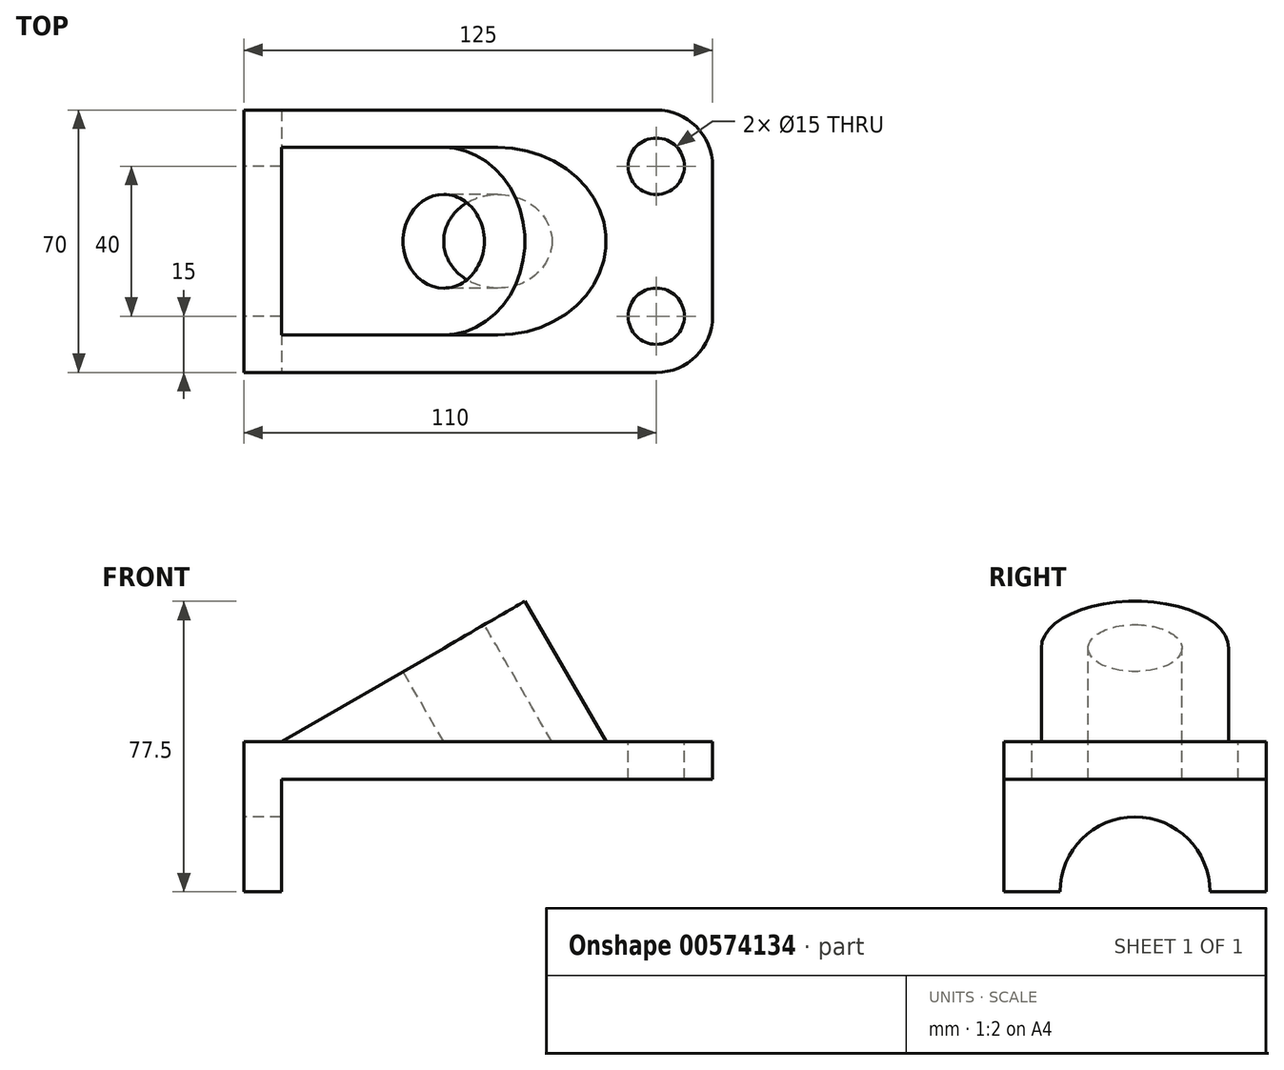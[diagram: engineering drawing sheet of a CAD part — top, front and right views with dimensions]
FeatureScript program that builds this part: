
annotation { "Feature Type Name" : "Feature", "Feature Type Description" : "" }
export const myFeature = defineFeature(function(context is Context, id is Id, definition is map)
    precondition{}
    {
        {
            var Q0;
            Q0=qCreatedBy(makeId("Front.planeOp"),FACE);
            var sketch = newSketch(context, id + "F0", { "sketchPlane" : qUnion([Q0])});
            skLineSegment(sketch, "E0.bottom", {"start": v(62.5, 20) * mm, "end": v(-62.5, 20) * mm});
            skLineSegment(sketch, "E0.top", {"start": v(62.5, -20) * mm, "end": v(-62.5, -20) * mm});
            skLineSegment(sketch, "E0.left", {"start": v(62.5, 20) * mm, "end": v(62.5, -20) * mm});
            skLineSegment(sketch, "E0.right", {"start": v(-62.5, 20) * mm, "end": v(-62.5, -20) * mm});
            skPoint(sketch, "E0.middle", {"position": v(0, 0) * mm});
            skSolve(sketch);
        }
        {
            var Q0;
            Q0=makeQuery(id+"F0.imprint","IMPRINT",FACE,{"disambiguationData":[TD([[makeQuery(id+"F0.imprint","IMPRINT",EDGE,{"derivedFrom":sQuery(id+"F0.wireOp",EDGE,"E0.bottom")}),1.0]])]});
            extrude(context, id + "F1", {"entities" : qUnion([Q0]), "depth" : 70 * mm, "offsetDistance" : 25 * mm});
        }
        {
            var Q0;
            Q0=makeQuery(id+"F1.opExtrude","SWEPT_FACE",FACE,{"disambiguationData":[OSD([sQuery(id+"F0.wireOp",EDGE,"E0.right")])]});
            var sketch = newSketch(context, id + "F2", { "sketchPlane" : qUnion([Q0])});
            skLineSegment(sketch, "E1", {"start": v(35, -20) * mm, "end": v(35, 0) * mm, "construction": true});
            skCircle(sketch, "E2", {"center": v(35, -20) * mm, "radius": 20 * mm});
            skLineSegment(sketch, "E3", {"start": v(0, -20) * mm, "end": v(15, -20) * mm, "construction": true});
            skLineSegment(sketch, "E4", {"start": v(70, -20) * mm, "end": v(55, -20) * mm, "construction": true});
            skSolve(sketch);
        }
        {
            var Q0;
            {var subQ0=sQuery(id+"F2.wireOp",EDGE,"E2");var subQ1=makeQuery(id+"F1.opExtrude","SWEPT_EDGE",EDGE,{"disambiguationData":[OSD([sQuery(id+"F0.wireOp",EDGE,"E0.top"),sQuery(id+"F0.wireOp",EDGE,"E0.right")])]});var subQ2=makeQuery(id+"F2.imprint","INTERSECT",VERTEX,{"disambiguationData":[OD(0.0)],"derivedFrom":[subQ1,subQ0]});Q0=makeQuery(id+"F2.imprint","IMPRINT",FACE,{"disambiguationData":[TD([[makeQuery(id+"F2.imprint","IMPRINT",EDGE,{"disambiguationData":[TD([[subQ2,1.0]])],"derivedFrom":subQ0}),1.0]])]});}
            var Q1;
            {var subQ0=sQuery(id+"F2.wireOp",EDGE,"E2");var subQ1=makeQuery(id+"F1.opExtrude","SWEPT_EDGE",EDGE,{"disambiguationData":[OSD([sQuery(id+"F0.wireOp",EDGE,"E0.top"),sQuery(id+"F0.wireOp",EDGE,"E0.right")])]});var subQ2=makeQuery(id+"F2.imprint","INTERSECT",VERTEX,{"disambiguationData":[OD(0.0)],"derivedFrom":[subQ1,subQ0]});Q1=makeQuery(id+"F2.imprint","IMPRINT",FACE,{"disambiguationData":[TD([[makeQuery(id+"F2.imprint","IMPRINT",EDGE,{"disambiguationData":[TD([[subQ2,-1.0]])],"derivedFrom":subQ0}),1.0]])]});}
            extrude(context, id + "F3", {"entities" : qUnion([Q0, Q1]), "operationType" : NewBodyOperationType.REMOVE, "endBound" : BoundingType.THROUGH_ALL, "oppositeDirection" : true, "depth" : 25 * mm, "offsetDistance" : 25 * mm});
        }
        {
            var Q0;
            Q0=makeQuery(id+"F1.opExtrude","CAP_FACE",FACE,{"disambiguationData":[OSD([sQuery(id+"F0.wireOp",EDGE,"E0.bottom"),sQuery(id+"F0.wireOp",EDGE,"E0.top"),sQuery(id+"F0.wireOp",EDGE,"E0.left"),sQuery(id+"F0.wireOp",EDGE,"E0.right")])],"isStart":false});
            var sketch = newSketch(context, id + "F4", { "sketchPlane" : qUnion([Q0])});
            skLineSegment(sketch, "E5", {"start": v(-62.5, -20) * mm, "end": v(-52.5, -20) * mm});
            skLineSegment(sketch, "E6", {"start": v(-52.5, -20) * mm, "end": v(-52.5, 10) * mm});
            skLineSegment(sketch, "E7", {"start": v(-52.5, 10) * mm, "end": v(62.5, 10) * mm});
            skSolve(sketch);
        }
        {
            var Q0;
            {var subQ0=sQuery(id+"F4.wireOp",EDGE,"E6");Q0=makeQuery(id+"F4.imprint","IMPRINT",FACE,{"disambiguationData":[TD([[makeQuery(id+"F4.imprint","IMPRINT",EDGE,{"derivedFrom":subQ0}),-1.0]])]});}
            extrude(context, id + "F5", {"entities" : qUnion([Q0]), "operationType" : NewBodyOperationType.REMOVE, "endBound" : BoundingType.THROUGH_ALL, "oppositeDirection" : true, "depth" : 25 * mm, "offsetDistance" : 25 * mm});
        }
        {
            var Q0;
            Q0=makeQuery(id+"F1.opExtrude","CAP_EDGE",EDGE,{"disambiguationData":[OSD([sQuery(id+"F0.wireOp",EDGE,"E0.left")])],"isStart":false});
            var Q1;
            Q1=makeQuery(id+"F1.opExtrude","CAP_EDGE",EDGE,{"disambiguationData":[OSD([sQuery(id+"F0.wireOp",EDGE,"E0.left")])],"isStart":true});
            fillet(context, id + "F6", {"entities" : qUnion([Q0, Q1]), "radius" : 15 * mm, "tangentPropagation" : true, "allowEdgeOverflow" : false});
        }
        {
            var Q0;
            Q0=makeQuery(id+"F1.opExtrude","SWEPT_FACE",FACE,{"disambiguationData":[OSD([sQuery(id+"F0.wireOp",EDGE,"E0.bottom")])]});
            var sketch = newSketch(context, id + "F7", { "sketchPlane" : qUnion([Q0])});
            skLineSegment(sketch, "E8", {"start": v(62.5, -35) * mm, "end": v(-62.5, -35) * mm, "construction": true});
            skLineSegment(sketch, "E9", {"start": v(47.5, -35) * mm, "end": v(47.5, -15) * mm, "construction": true});
            skCircle(sketch, "E10", {"center": v(47.5, -15) * mm, "radius": 7.5 * mm});
            skCircle(sketch, "E11.MirrorC", {"center": v(47.5, -55) * mm, "radius": 7.5 * mm});
            skSolve(sketch);
        }
        {
            var Q0;
            Q0 = qSketchRegion(id + "F7", true);
            extrude(context, id + "F8", {"entities" : qUnion([Q0]), "operationType" : NewBodyOperationType.REMOVE, "endBound" : BoundingType.THROUGH_ALL, "oppositeDirection" : true, "depth" : 25 * mm, "offsetDistance" : 25 * mm});
        }
        {
            var Q0;
            Q0=makeQuery(id+"F1.opExtrude","CAP_FACE",FACE,{"disambiguationData":[OSD([sQuery(id+"F0.wireOp",EDGE,"E0.bottom"),sQuery(id+"F0.wireOp",EDGE,"E0.top"),sQuery(id+"F0.wireOp",EDGE,"E0.left"),sQuery(id+"F0.wireOp",EDGE,"E0.right")])],"isStart":false});
            cPlane(context, id + "F9", {"entities" : qUnion([Q0]), "cplaneType" : CPlaneType.OFFSET, "offset" : 10 * mm, "oppositeDirection" : true, "width" : 150 * mm, "height" : 150 * mm});
        }
        {
            var Q0;
            Q0=qCreatedBy(id+"F9.planeOp",FACE);
            var sketch = newSketch(context, id + "F10", { "sketchPlane" : qUnion([Q0])});
            skLineSegment(sketch, "E12", {"start": v(-62.5, 0) * mm, "end": v(-62.5, 20) * mm, "construction": true});
            skLineSegment(sketch, "E13", {"start": v(-62.5, 20) * mm, "end": v(-52.5, 20) * mm, "construction": true});
            skLineSegment(sketch, "E14", {"start": v(-52.5, 20) * mm, "end": v(12.45, 57.5) * mm});
            skLineSegment(sketch, "E15", {"start": v(12.45, 57.5) * mm, "end": v(34.1, 20) * mm});
            skLineSegment(sketch, "E16", {"start": v(-52.5, 20) * mm, "end": v(34.1, 20) * mm});
            skSolve(sketch);
        }
        {
            var Q0;
            Q0 = qSketchRegion(id + "F10", true);
            extrude(context, id + "F11", {"entities" : qUnion([Q0]), "operationType" : NewBodyOperationType.ADD, "oppositeDirection" : true, "depth" : 50 * mm, "offsetDistance" : 25 * mm});
        }
        {
            var Q0;
            Q0=makeQuery(id+"F11.opExtrude","SWEPT_FACE",FACE,{"disambiguationData":[OSD([sQuery(id+"F10.wireOp",EDGE,"E14")])]});
            var sketch = newSketch(context, id + "F12", { "sketchPlane" : qUnion([Q0])});
            skLineSegment(sketch, "E17", {"start": v(-35.47, -60) * mm, "end": v(-35.47, -35) * mm, "construction": true});
            skLineSegment(sketch, "E18", {"start": v(-35.47, -35) * mm, "end": v(14.53, -35) * mm, "construction": true});
            skArc(sketch, "E19", {"start": v(14.53, -60) * mm, "mid": v(39.53, -35) * mm, "end": v(14.53, -10) * mm});
            skLineSegment(sketch, "E20", {"start": v(14.53, -69.81) * mm, "end": v(14.53, -60) * mm});
            skLineSegment(sketch, "E21", {"start": v(14.53, 5.52) * mm, "end": v(54.42, 5.52) * mm});
            skLineSegment(sketch, "E22", {"start": v(54.42, 5.52) * mm, "end": v(54.42, -77.32) * mm});
            skLineSegment(sketch, "E23", {"start": v(54.42, -77.32) * mm, "end": v(14.53, -77.32) * mm});
            skLineSegment(sketch, "E24", {"start": v(14.53, -77.32) * mm, "end": v(14.53, -69.81) * mm});
            skLineSegment(sketch, "E25.trimOffspring", {"start": v(14.53, -10) * mm, "end": v(14.53, 5.52) * mm});
            skSolve(sketch);
        }
        {
            var Q0;
            {var subQ0=sQuery(id+"F12.wireOp",EDGE,"E19");var subQ1=sQuery(id+"F10.wireOp",EDGE,"E14");var subQ2=makeQuery(id+"F11.opExtrude","CAP_EDGE",EDGE,{"disambiguationData":[OSD([subQ1])],"isStart":true});var subQ3=makeQuery(id+"F12.imprint","INTERSECT",VERTEX,{"derivedFrom":[subQ2,subQ0,sQuery(id+"F12.wireOp",EDGE,"E20")]});Q0=makeQuery(id+"F12.imprint","IMPRINT",FACE,{"disambiguationData":[TD([[makeQuery(id+"F12.imprint","IMPRINT",EDGE,{"disambiguationData":[TD([[subQ3,-1.0]])],"derivedFrom":subQ0}),-1.0]])]});}
            var Q1;
            {var subQ0=sQuery(id+"F12.wireOp",EDGE,"E19");var subQ1=sQuery(id+"F10.wireOp",EDGE,"E14");var subQ2=makeQuery(id+"F11.opExtrude","CAP_EDGE",EDGE,{"disambiguationData":[OSD([subQ1])],"isStart":false});var subQ3=makeQuery(id+"F12.imprint","INTERSECT",VERTEX,{"derivedFrom":[subQ2,subQ0,sQuery(id+"F12.wireOp",EDGE,"E25.trimOffspring")]});Q1=makeQuery(id+"F12.imprint","IMPRINT",FACE,{"disambiguationData":[TD([[makeQuery(id+"F12.imprint","IMPRINT",EDGE,{"disambiguationData":[TD([[subQ3,1.0]])],"derivedFrom":subQ0}),-1.0]])]});}
            var Q2;
            Q2=makeQuery(id+"F1.opExtrude","SWEPT_FACE",FACE,{"disambiguationData":[OSD([sQuery(id+"F0.wireOp",EDGE,"E0.bottom")])]});
            extrude(context, id + "F13", {"entities" : qUnion([Q0, Q1]), "operationType" : NewBodyOperationType.REMOVE, "endBound" : BoundingType.UP_TO_SURFACE, "oppositeDirection" : true, "depth" : 25 * mm, "endBoundEntityFace" : qUnion([Q2]), "offsetDistance" : 25 * mm});
        }
        {
            var Q0;
            Q0=makeQuery(id+"F11.opExtrude","SWEPT_FACE",FACE,{"disambiguationData":[OSD([sQuery(id+"F10.wireOp",EDGE,"E14")])]});
            var sketch = newSketch(context, id + "F14", { "sketchPlane" : qUnion([Q0])});
            skCircle(sketch, "E26", {"center": v(14.53, -35) * mm, "radius": 12.5 * mm});
            skSolve(sketch);
        }
        {
            var Q0;
            Q0=makeQuery(id+"F14.imprint","IMPRINT",FACE,{"disambiguationData":[TD([[makeQuery(id+"F14.imprint","IMPRINT",EDGE,{"derivedFrom":sQuery(id+"F14.wireOp",EDGE,"E26")}),1.0]])]});
            var Q1;
            {var subQ0=sQuery(id+"F0.wireOp",EDGE,"E0.bottom");Q1=makeQuery(id+"F13.boolean.opBoolean","MERGE",FACE,{"derivedFrom":[makeQuery(id+"F1.opExtrude","SWEPT_FACE",FACE,{"disambiguationData":[OSD([subQ0])]}),makeQuery(id+"F13.opExtrude","CAP_FACE",FACE,{"disambiguationData":[OSD([subQ0]),OD(0.0)],"isStart":false}),makeQuery(id+"F13.opExtrude","CAP_FACE",FACE,{"disambiguationData":[OSD([subQ0]),OD(1.0)],"isStart":false})]});}
            extrude(context, id + "F15", {"entities" : qUnion([Q0]), "operationType" : NewBodyOperationType.REMOVE, "endBound" : BoundingType.UP_TO_SURFACE, "oppositeDirection" : true, "depth" : 25 * mm, "endBoundEntityFace" : qUnion([Q1]), "offsetDistance" : 25 * mm});
        }
    });
